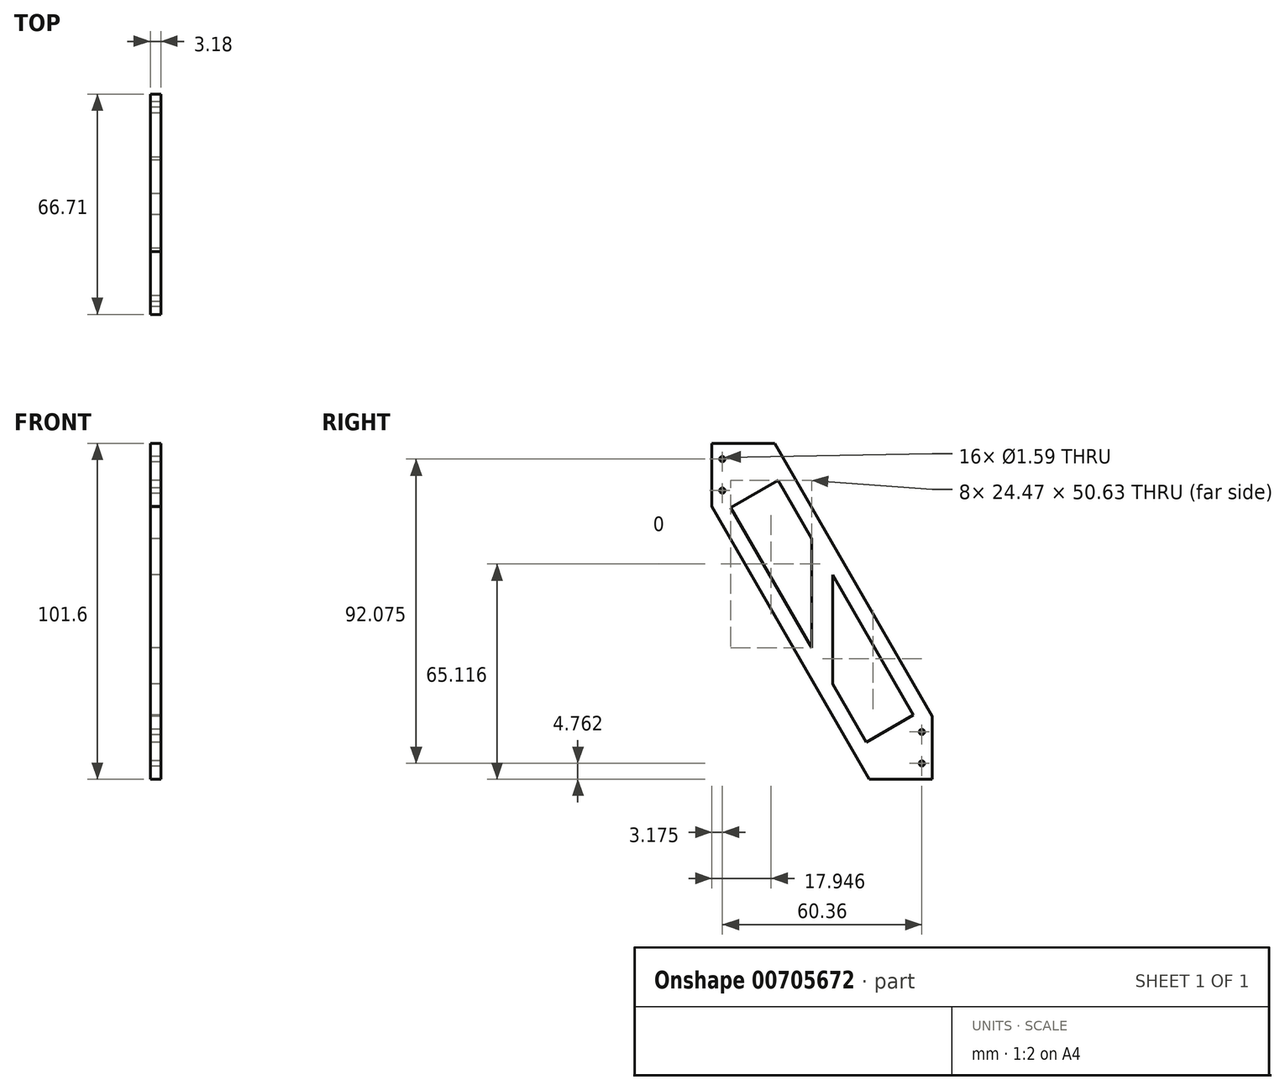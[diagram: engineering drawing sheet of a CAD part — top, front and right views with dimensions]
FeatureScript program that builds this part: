
annotation { "Feature Type Name" : "Feature", "Feature Type Description" : "" }
export const myFeature = defineFeature(function(context is Context, id is Id, definition is map)
    precondition{}
    {
        {
            var Q0;
            Q0=qCreatedBy(makeId("Right.planeOp"),FACE);
            var sketch = newSketch(context, id + "F0", { "sketchPlane" : qUnion([Q0])});
            skLineSegment(sketch, "E0", {"start": v(0, 0) * mm, "end": v(0, -19.05) * mm});
            skLineSegment(sketch, "E1", {"start": v(0, -19.05) * mm, "end": v(47.66, -101.6) * mm});
            skLineSegment(sketch, "E2", {"start": v(47.66, -101.6) * mm, "end": v(66.71, -101.6) * mm});
            skLineSegment(sketch, "E3", {"start": v(66.71, -101.6) * mm, "end": v(66.71, -82.55) * mm});
            skLineSegment(sketch, "E4", {"start": v(0, 0) * mm, "end": v(19.05, 0) * mm});
            skLineSegment(sketch, "E5", {"start": v(19.05, 0) * mm, "end": v(66.71, -82.55) * mm});
            skCircle(sketch, "E6", {"center": v(3.17, -4.76) * mm, "radius": 0.8 * mm});
            skCircle(sketch, "E7", {"center": v(3.18, -14.29) * mm, "radius": 0.8 * mm});
            skCircle(sketch, "E8", {"center": v(63.54, -87.31) * mm, "radius": 0.8 * mm});
            skCircle(sketch, "E9", {"center": v(63.54, -96.84) * mm, "radius": 0.8 * mm});
            skLineSegment(sketch, "E10", {"start": v(63.54, -87.31) * mm, "end": v(63.54, -96.84) * mm, "construction": true});
            skLineSegment(sketch, "E11", {"start": v(63.54, -96.84) * mm, "end": v(63.54, -101.6) * mm, "construction": true});
            skLineSegment(sketch, "E12", {"start": v(3.18, -14.29) * mm, "end": v(3.17, -4.76) * mm, "construction": true});
            skLineSegment(sketch, "E13", {"start": v(3.17, -4.76) * mm, "end": v(3.17, 0) * mm, "construction": true});
            skLineSegment(sketch, "E14", {"start": v(5.71, -19.42) * mm, "end": v(20, -11.17) * mm});
            skLineSegment(sketch, "E15", {"start": v(20, -11.17) * mm, "end": v(30.18, -28.8) * mm});
            skLineSegment(sketch, "E16", {"start": v(30.18, -28.8) * mm, "end": v(30.18, -61.8) * mm});
            skLineSegment(sketch, "E17", {"start": v(30.18, -61.8) * mm, "end": v(5.71, -19.42) * mm});
            skLineSegment(sketch, "E18", {"start": v(36.53, -39.8) * mm, "end": v(36.53, -72.8) * mm});
            skLineSegment(sketch, "E19", {"start": v(36.53, -72.8) * mm, "end": v(46.71, -90.43) * mm});
            skLineSegment(sketch, "E20", {"start": v(46.71, -90.43) * mm, "end": v(61, -82.18) * mm});
            skLineSegment(sketch, "E21", {"start": v(61, -82.18) * mm, "end": v(36.53, -39.8) * mm});
            skSolve(sketch);
        }
        {
            var Q0;
            Q0=makeQuery(id+"F0.imprint","IMPRINT",FACE,{"disambiguationData":[TD([[makeQuery(id+"F0.imprint","IMPRINT",EDGE,{"derivedFrom":sQuery(id+"F0.wireOp",EDGE,"E0")}),1.0]])]});
            extrude(context, id + "F1", {"entities" : qUnion([Q0]), "depth" : 3.17 * mm, "offsetDistance" : 25.4 * mm});
        }
    });
